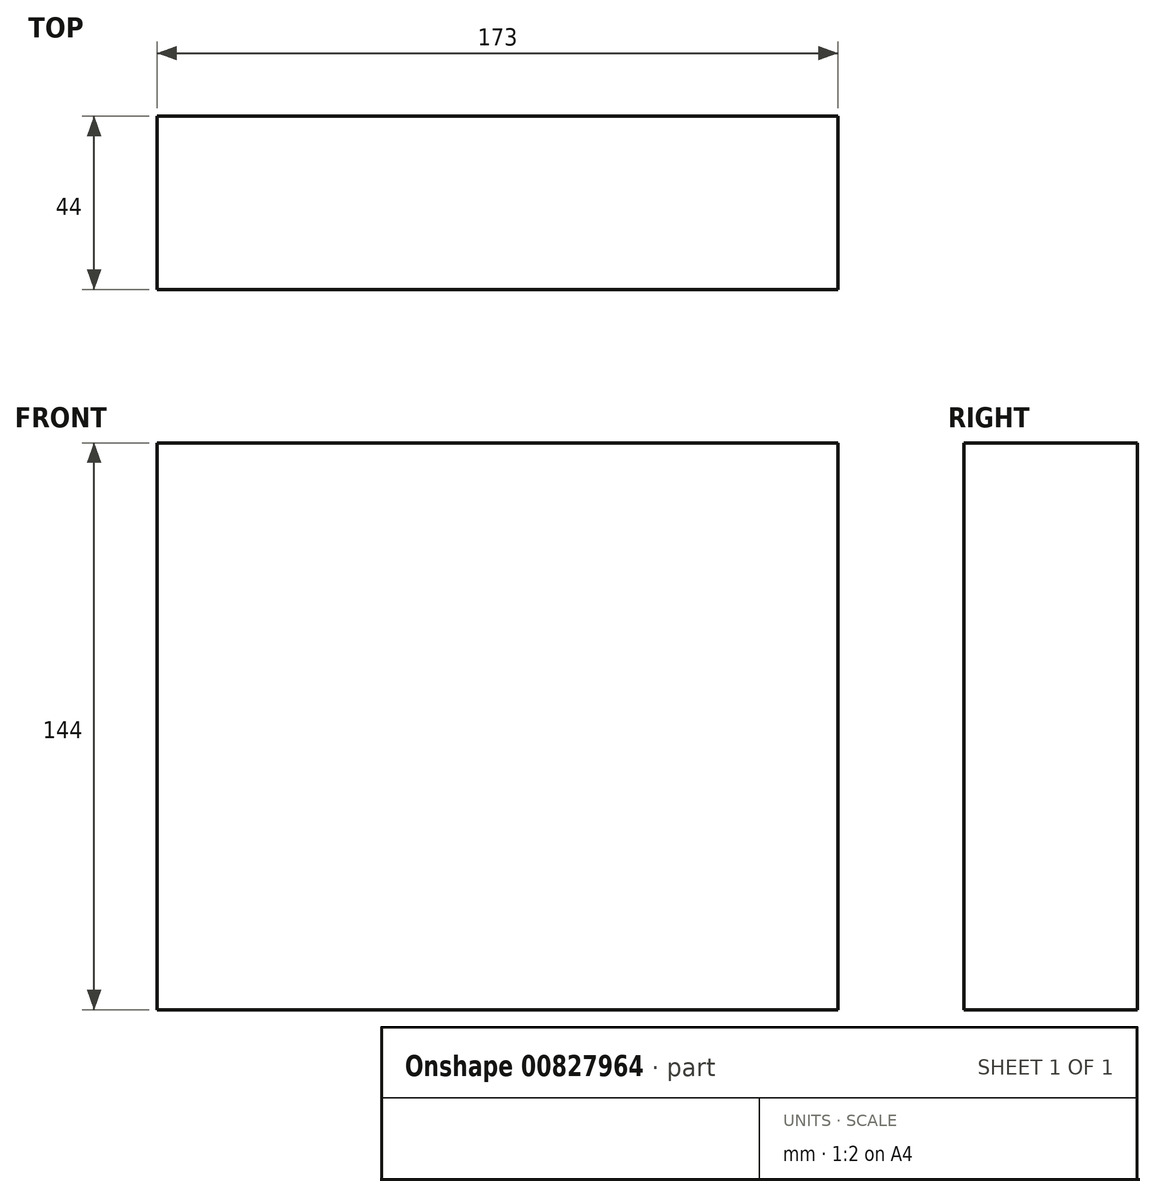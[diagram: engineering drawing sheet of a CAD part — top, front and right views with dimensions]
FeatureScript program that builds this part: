
annotation { "Feature Type Name" : "Feature", "Feature Type Description" : "" }
export const myFeature = defineFeature(function(context is Context, id is Id, definition is map)
    precondition{}
    {
        {
            var Q0;
            Q0=qCreatedBy(makeId("Top.planeOp"),FACE);
            var sketch = newSketch(context, id + "F0", { "sketchPlane" : qUnion([Q0])});
            skLineSegment(sketch, "E0.bottom", {"start": v(-86.5, 22) * mm, "end": v(86.5, 22) * mm});
            skLineSegment(sketch, "E0.top", {"start": v(-86.5, -22) * mm, "end": v(86.5, -22) * mm});
            skLineSegment(sketch, "E0.left", {"start": v(-86.5, 22) * mm, "end": v(-86.5, -22) * mm});
            skLineSegment(sketch, "E0.right", {"start": v(86.5, 22) * mm, "end": v(86.5, -22) * mm});
            skPoint(sketch, "E0.middle", {"position": v(0, 0) * mm});
            skSolve(sketch);
        }
        {
            var Q0;
            Q0=makeQuery(id+"F0.imprint","IMPRINT",FACE,{"disambiguationData":[TD([[makeQuery(id+"F0.imprint","IMPRINT",EDGE,{"derivedFrom":sQuery(id+"F0.wireOp",EDGE,"E0.bottom")}),-1.0]])]});
            extrude(context, id + "F1", {"entities" : qUnion([Q0]), "depth" : 144 * mm, "offsetDistance" : 25 * mm});
        }
    });
